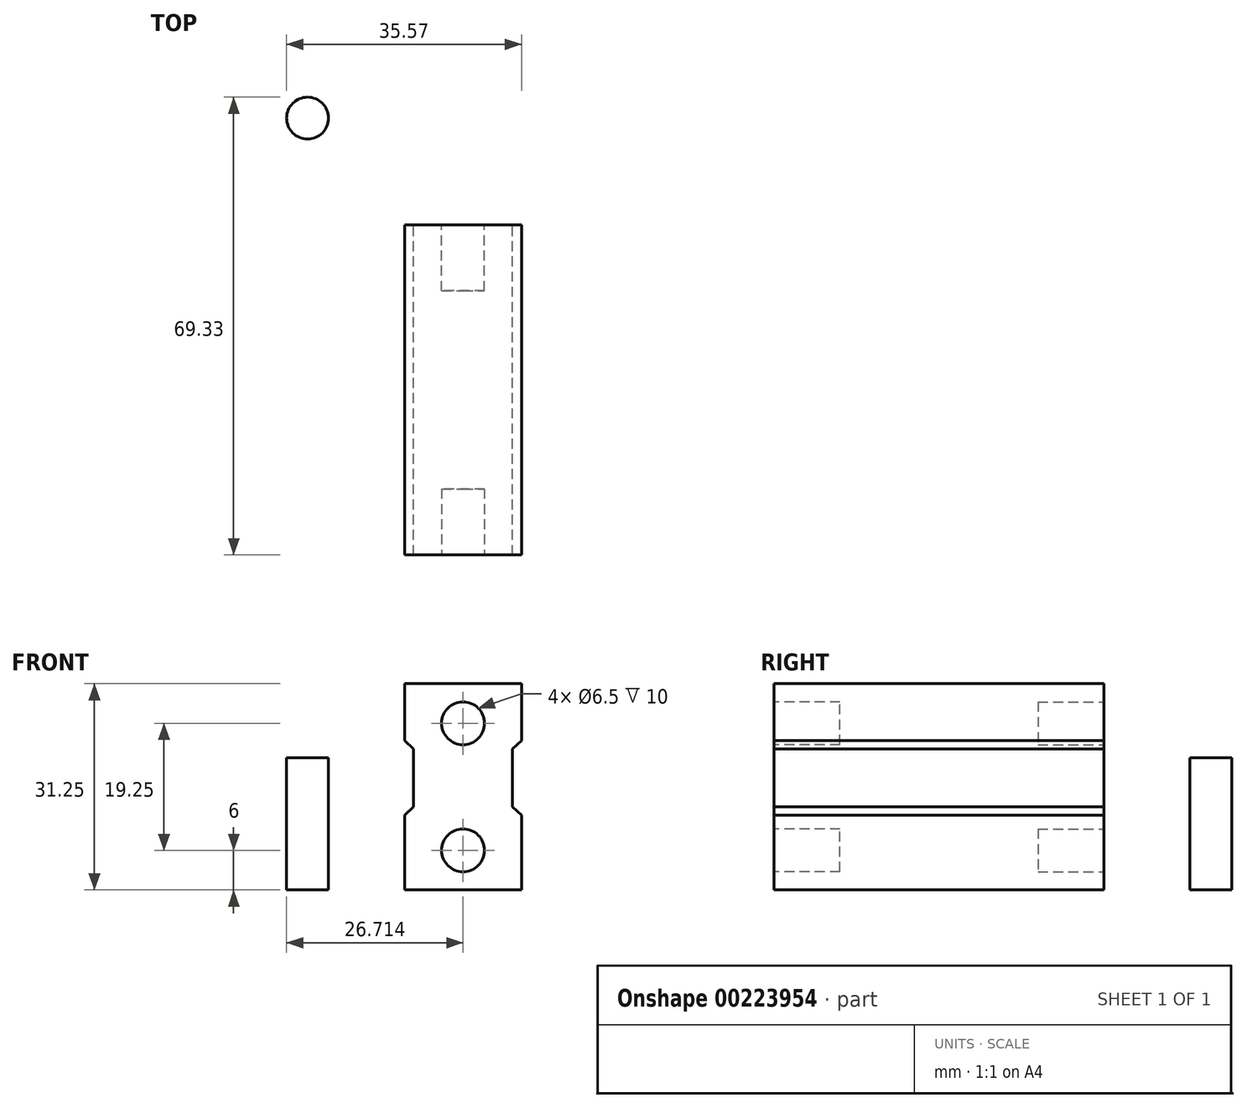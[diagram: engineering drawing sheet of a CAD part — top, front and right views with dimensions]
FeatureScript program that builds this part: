
annotation { "Feature Type Name" : "Feature", "Feature Type Description" : "" }
export const myFeature = defineFeature(function(context is Context, id is Id, definition is map)
    precondition{}
    {
        {
            var Q0;
            Q0=qCreatedBy(makeId("Front.planeOp"),FACE);
            var sketch = newSketch(context, id + "F0", { "sketchPlane" : qUnion([Q0])});
            skLineSegment(sketch, "E0.bottom", {"start": v(0, 0) * mm, "end": v(17.7, 0) * mm, "construction": true});
            skLineSegment(sketch, "E0.top", {"start": v(0, 31.25) * mm, "end": v(17.7, 31.25) * mm, "construction": true});
            skLineSegment(sketch, "E0.left", {"start": v(0, 0) * mm, "end": v(0, 31.25) * mm, "construction": true});
            skLineSegment(sketch, "E0.right", {"start": v(17.7, 0) * mm, "end": v(17.7, 31.25) * mm, "construction": true});
            skLineSegment(sketch, "E1", {"start": v(8.85, 31.25) * mm, "end": v(8.85, 0) * mm, "construction": true});
            skLineSegment(sketch, "E2", {"start": v(8.85, 0) * mm, "end": v(0, 0) * mm});
            skLineSegment(sketch, "E3", {"start": v(0, 11.35) * mm, "end": v(1.35, 12.6) * mm});
            skLineSegment(sketch, "E4", {"start": v(1.35, 12.6) * mm, "end": v(1.35, 21.35) * mm});
            skLineSegment(sketch, "E5", {"start": v(1.35, 21.35) * mm, "end": v(0, 22.6) * mm});
            skLineSegment(sketch, "E6", {"start": v(0, 22.6) * mm, "end": v(0, 31.25) * mm});
            skLineSegment(sketch, "E7", {"start": v(8.85, 31.25) * mm, "end": v(0, 31.25) * mm});
            skLineSegment(sketch, "E8", {"start": v(0, 0) * mm, "end": v(0, 11.35) * mm});
            skLineSegment(sketch, "E9.MirrorCS", {"start": v(16.35, 21.35) * mm, "end": v(17.7, 22.6) * mm});
            skLineSegment(sketch, "E10.MirrorCS", {"start": v(17.7, 11.35) * mm, "end": v(16.35, 12.6) * mm});
            skLineSegment(sketch, "E11.MirrorCS", {"start": v(17.7, 0) * mm, "end": v(17.7, 11.35) * mm});
            skLineSegment(sketch, "E12.MirrorCS", {"start": v(8.85, 31.25) * mm, "end": v(17.7, 31.25) * mm});
            skLineSegment(sketch, "E13.MirrorCS", {"start": v(8.85, 0) * mm, "end": v(17.7, 0) * mm});
            skLineSegment(sketch, "E14.MirrorCS", {"start": v(16.35, 12.6) * mm, "end": v(16.35, 21.35) * mm});
            skLineSegment(sketch, "E15.MirrorCS", {"start": v(17.7, 22.6) * mm, "end": v(17.7, 31.25) * mm});
            skSolve(sketch);
        }
        {
            var Q0;
            Q0=makeQuery(id+"F0.imprint","IMPRINT",FACE,{"disambiguationData":[TD([[makeQuery(id+"F0.imprint","IMPRINT",EDGE,{"derivedFrom":sQuery(id+"F0.wireOp",EDGE,"E2")}),-1.0]])]});
            extrude(context, id + "F1", {"entities" : qUnion([Q0]), "depth" : 50 * mm});
        }
        {
            var Q0;
            Q0=makeQuery(id+"F1.opExtrude","CAP_FACE",FACE,{"disambiguationData":[OSD([sQuery(id+"F0.wireOp",EDGE,"E2"),sQuery(id+"F0.wireOp",EDGE,"E3"),sQuery(id+"F0.wireOp",EDGE,"E4"),sQuery(id+"F0.wireOp",EDGE,"E5"),sQuery(id+"F0.wireOp",EDGE,"E6"),sQuery(id+"F0.wireOp",EDGE,"E7"),sQuery(id+"F0.wireOp",EDGE,"E8"),sQuery(id+"F0.wireOp",EDGE,"E9.MirrorCS"),sQuery(id+"F0.wireOp",EDGE,"E10.MirrorCS"),sQuery(id+"F0.wireOp",EDGE,"E11.MirrorCS"),sQuery(id+"F0.wireOp",EDGE,"E12.MirrorCS"),sQuery(id+"F0.wireOp",EDGE,"E13.MirrorCS"),sQuery(id+"F0.wireOp",EDGE,"E14.MirrorCS"),sQuery(id+"F0.wireOp",EDGE,"E15.MirrorCS")])],"isStart":false});
            var sketch = newSketch(context, id + "F2", { "sketchPlane" : qUnion([Q0])});
            skLineSegment(sketch, "E16.bottom", {"start": v(0, 31.25) * mm, "end": v(17.7, 31.25) * mm, "construction": true});
            skLineSegment(sketch, "E16.top", {"start": v(0, 0) * mm, "end": v(17.7, 0) * mm, "construction": true});
            skLineSegment(sketch, "E16.left", {"start": v(0, 31.25) * mm, "end": v(0, 0) * mm, "construction": true});
            skLineSegment(sketch, "E16.right", {"start": v(17.7, 31.25) * mm, "end": v(17.7, 0) * mm, "construction": true});
            skLineSegment(sketch, "E17", {"start": v(8.85, 31.25) * mm, "end": v(8.85, 0) * mm, "construction": true});
            skCircle(sketch, "E18", {"center": v(8.85, 6) * mm, "radius": 3.25 * mm});
            skCircle(sketch, "E19", {"center": v(8.85, 25.25) * mm, "radius": 3.25 * mm});
            skSolve(sketch);
        }
        {
            var Q0;
            Q0 = qSketchRegion(id + "F2", true);
            extrude(context, id + "F3", {"entities" : qUnion([Q0]), "operationType" : NewBodyOperationType.REMOVE, "oppositeDirection" : true, "depth" : 10 * mm});
        }
        {
            var Q0;
            Q0=makeQuery(id+"F1.opExtrude","CAP_FACE",FACE,{"disambiguationData":[OSD([sQuery(id+"F0.wireOp",EDGE,"E2"),sQuery(id+"F0.wireOp",EDGE,"E3"),sQuery(id+"F0.wireOp",EDGE,"E4"),sQuery(id+"F0.wireOp",EDGE,"E5"),sQuery(id+"F0.wireOp",EDGE,"E6"),sQuery(id+"F0.wireOp",EDGE,"E7"),sQuery(id+"F0.wireOp",EDGE,"E8"),sQuery(id+"F0.wireOp",EDGE,"E9.MirrorCS"),sQuery(id+"F0.wireOp",EDGE,"E10.MirrorCS"),sQuery(id+"F0.wireOp",EDGE,"E11.MirrorCS"),sQuery(id+"F0.wireOp",EDGE,"E12.MirrorCS"),sQuery(id+"F0.wireOp",EDGE,"E13.MirrorCS"),sQuery(id+"F0.wireOp",EDGE,"E14.MirrorCS"),sQuery(id+"F0.wireOp",EDGE,"E15.MirrorCS")])],"isStart":true});
            var sketch = newSketch(context, id + "F4", { "sketchPlane" : qUnion([Q0])});
            skLineSegment(sketch, "E20.bottom", {"start": v(-17.7, 31.25) * mm, "end": v(0, 31.25) * mm, "construction": true});
            skLineSegment(sketch, "E20.top", {"start": v(-17.7, 0) * mm, "end": v(0, 0) * mm, "construction": true});
            skLineSegment(sketch, "E20.left", {"start": v(-17.7, 31.25) * mm, "end": v(-17.7, 0) * mm, "construction": true});
            skLineSegment(sketch, "E20.right", {"start": v(0, 31.25) * mm, "end": v(0, 0) * mm, "construction": true});
            skLineSegment(sketch, "E21", {"start": v(-8.85, 31.25) * mm, "end": v(-8.85, 0) * mm, "construction": true});
            skCircle(sketch, "E22", {"center": v(-8.85, 6) * mm, "radius": 3.25 * mm});
            skCircle(sketch, "E23", {"center": v(-8.85, 25.25) * mm, "radius": 3.25 * mm});
            skSolve(sketch);
        }
        {
            var Q0;
            Q0 = qSketchRegion(id + "F4", true);
            extrude(context, id + "F5", {"entities" : qUnion([Q0]), "operationType" : NewBodyOperationType.REMOVE, "oppositeDirection" : true, "depth" : 10 * mm});
        }
        {
            var Q0;
            Q0=qCreatedBy(makeId("Top.planeOp"),FACE);
            var sketch = newSketch(context, id + "F6", { "sketchPlane" : qUnion([Q0])});
            skCircle(sketch, "E24", {"center": v(-14.69, 16.16) * mm, "radius": 3.18 * mm});
            skSolve(sketch);
        }
        {
            var Q0;
            Q0=makeQuery(id+"F6.imprint","IMPRINT",FACE,{"disambiguationData":[TD([[makeQuery(id+"F6.imprint","IMPRINT",EDGE,{"derivedFrom":sQuery(id+"F6.wireOp",EDGE,"E24")}),1.0]])]});
            extrude(context, id + "F7", {"entities" : qUnion([Q0]), "depth" : 20 * mm});
        }
    });
